# Revit family: LES10B10
name_source: partatom
category: Detail Items
revit_build: Autodesk Revit 2015 (Build: 20140606_1530(x64)
units: mm (PartAtom-declared; Revit-internal decimal feet)

## types (4) — shared parameters
Density = 0.30 kg
Description = Connector Other
EPD = https://www.strongtie.eu
ETA / DoP = https://www.strongtie.eu
Manufacturer = Simpson Strong-Tie
Model = LES10B10
Model Disclaimer = Contact Simpson Strong-Tie Company  for more information
Model ID = 0144542475555036698145310495330263353632
Name = LES10B10
ObjectType = LES10B10
Product Material = Galvanised
Product Type = Connector Other
Reference = LES10B10
Technical datasheet = https://www.strongtie.eu
URL = www.strongtie.eu
UniClass Number = Pr_20_29_31_44
UniClass Title = Joist hangers

## per-type parameters (varying)
| type | _visiblefront | _visibleleft | _visibleright | _visibletop |
| SST_LES10B10_Right | No | No | Yes | No |
| SST_LES10B10_Front | Yes | No | No | No |
| SST_LES10B10_Top | No | No | No | Yes |
| SST_LES10B10_Left | No | Yes | No | No |
